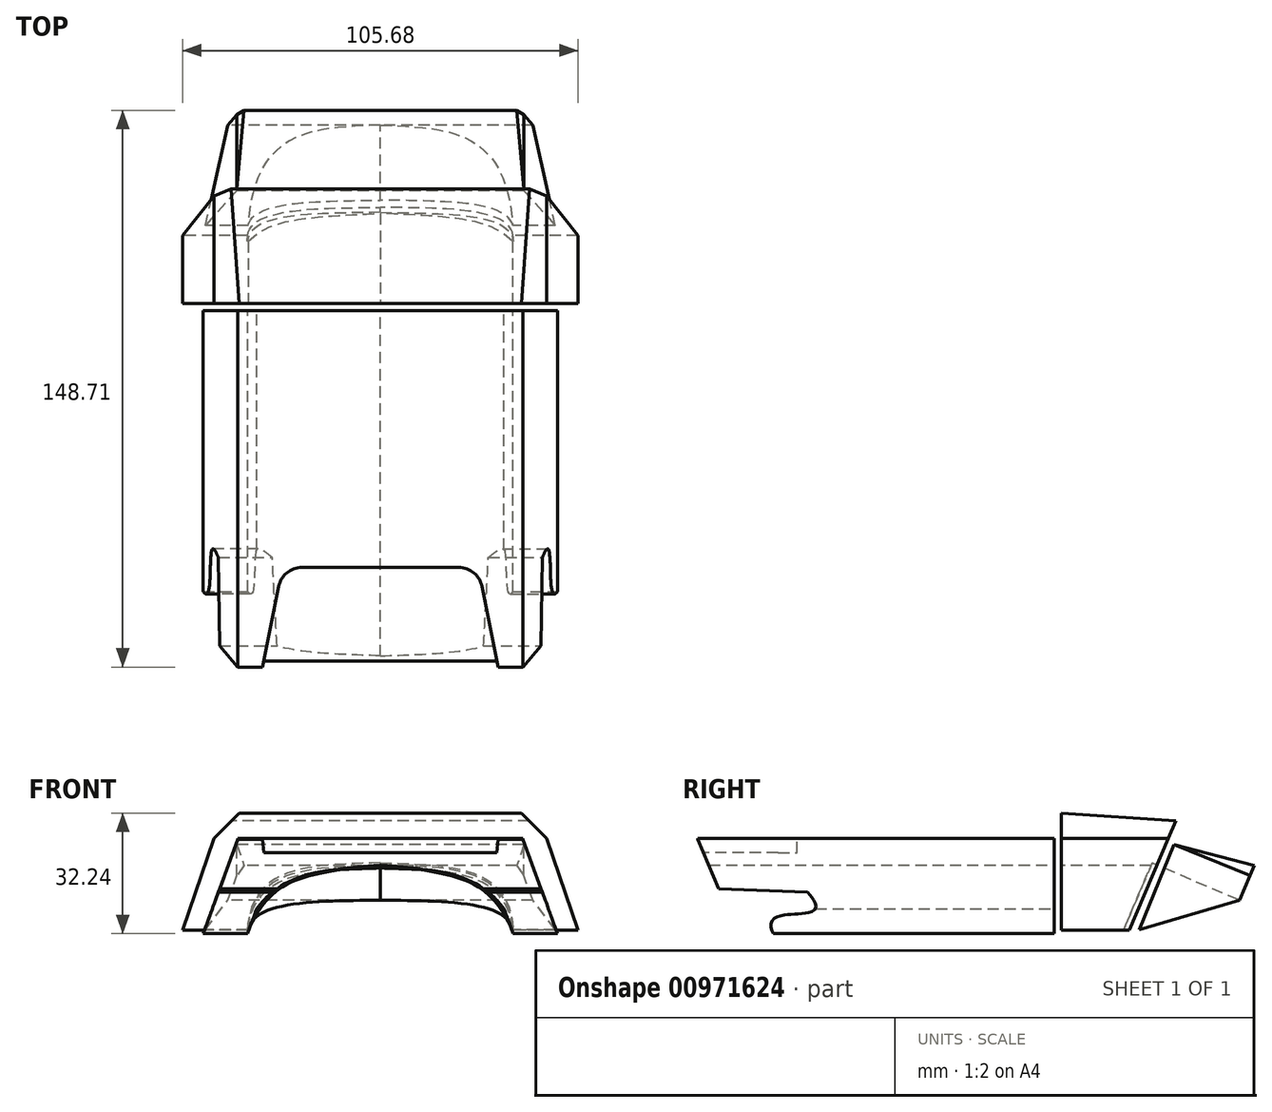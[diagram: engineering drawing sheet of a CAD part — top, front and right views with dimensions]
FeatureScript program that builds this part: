
annotation { "Feature Type Name" : "Feature", "Feature Type Description" : "" }
export const myFeature = defineFeature(function(context is Context, id is Id, definition is map)
    precondition{}
    {
        {
            var Q0;
            Q0=qCreatedBy(makeId("Top.planeOp"),FACE);
            var sketch = newSketch(context, id + "F0", { "sketchPlane" : qUnion([Q0])});
            skLineSegment(sketch, "E0.bottom", {"start": v(38.1, 47.63) * mm, "end": v(-38.1, 47.63) * mm});
            skLineSegment(sketch, "E0.top", {"start": v(38.1, -47.63) * mm, "end": v(-38.1, -47.63) * mm});
            skLineSegment(sketch, "E0.left", {"start": v(38.1, 47.63) * mm, "end": v(38.1, -47.63) * mm});
            skLineSegment(sketch, "E0.right", {"start": v(-38.1, 47.63) * mm, "end": v(-38.1, -47.63) * mm});
            skPoint(sketch, "E0.middle", {"position": v(0, 0) * mm});
            skLineSegment(sketch, "E1", {"start": v(0, -21.05) * mm, "end": v(-20.94, -21.05) * mm});
            skLineSegment(sketch, "E2", {"start": v(-27.17, -26.16) * mm, "end": v(-31.46, -47.63) * mm});
            skPoint(sketch, "E3.visualSharp", {"position": v(-26.15, -21.05) * mm});
            skArc(sketch, "E3.filletArc", {"start": v(-20.94, -21.05) * mm, "mid": v(-24.96, -22.5) * mm, "end": v(-27.17, -26.16) * mm});
            skLineSegment(sketch, "E4.MirrorCS", {"start": v(0, -21.05) * mm, "end": v(20.94, -21.05) * mm});
            skArc(sketch, "E5.MirrorCS", {"start": v(20.94, -21.05) * mm, "mid": v(24.96, -22.5) * mm, "end": v(27.17, -26.16) * mm});
            skLineSegment(sketch, "E6.MirrorCS", {"start": v(27.17, -26.16) * mm, "end": v(31.46, -47.63) * mm});
            skSolve(sketch);
        }
        {
            var Q0;
            Q0=makeQuery(id+"F0.imprint","IMPRINT",FACE,{"disambiguationData":[TD([[makeQuery(id+"F0.imprint","IMPRINT",EDGE,{"derivedFrom":sQuery(id+"F0.wireOp",EDGE,"E0.bottom")}),1.0]])]});
            var Q1;
            Q1=makeQuery(id+"F0.imprint","IMPRINT",FACE,{"disambiguationData":[TD([[makeQuery(id+"F0.imprint","IMPRINT",EDGE,{"derivedFrom":sQuery(id+"F0.wireOp",EDGE,"E1")}),1.0]])]});
            extrude(context, id + "F1", {"entities" : qUnion([Q0, Q1]), "oppositeDirection" : true, "depth" : 25.4 * mm, "offsetDistance" : 25.4 * mm, "hasDraft" : true, "draftAngle" : 20 * degree});
        }
        {
            var Q0;
            Q0=makeQuery(id+"F1.opExtrude","CAP_FACE",FACE,{"disambiguationData":[OSD([sQuery(id+"F0.wireOp",EDGE,"E0.bottom"),sQuery(id+"F0.wireOp",EDGE,"E0.top"),sQuery(id+"F0.wireOp",EDGE,"E0.left"),sQuery(id+"F0.wireOp",EDGE,"E0.right")])],"isStart":true});
            var sketch = newSketch(context, id + "F2", { "sketchPlane" : qUnion([Q0])});
            skLineSegment(sketch, "E7.bottom", {"start": v(-53.4, 47.63) * mm, "end": v(63.46, 47.63) * mm});
            skLineSegment(sketch, "E7.top", {"start": v(-53.4, 69.25) * mm, "end": v(63.46, 69.25) * mm});
            skLineSegment(sketch, "E7.left", {"start": v(-53.4, 47.63) * mm, "end": v(-53.4, 69.25) * mm});
            skLineSegment(sketch, "E7.right", {"start": v(63.46, 47.63) * mm, "end": v(63.46, 69.25) * mm});
            skLineSegment(sketch, "E8.bottom", {"start": v(-38.1, -47.63) * mm, "end": v(-66.4, -47.63) * mm});
            skLineSegment(sketch, "E8.top", {"start": v(-38.1, -70.22) * mm, "end": v(-66.4, -70.22) * mm});
            skLineSegment(sketch, "E8.left", {"start": v(-38.1, -47.63) * mm, "end": v(-38.1, -70.22) * mm});
            skLineSegment(sketch, "E8.right", {"start": v(-66.4, -47.63) * mm, "end": v(-66.4, -70.22) * mm});
            skLineSegment(sketch, "E9.bottom", {"start": v(-38.1, -47.63) * mm, "end": v(69.23, -47.63) * mm});
            skLineSegment(sketch, "E9.top", {"start": v(-38.1, -70.22) * mm, "end": v(69.23, -70.22) * mm});
            skLineSegment(sketch, "E9.right", {"start": v(69.23, -47.63) * mm, "end": v(69.23, -70.22) * mm});
            skSolve(sketch);
        }
        {
            var Q0;
            Q0=makeQuery(id+"F2.imprint","IMPRINT",FACE,{"disambiguationData":[TD([[makeQuery(id+"F2.imprint","IMPRINT",EDGE,{"derivedFrom":sQuery(id+"F2.wireOp",EDGE,"E9.top")}),1.0]])]});
            var Q1;
            Q1=makeQuery(id+"F2.imprint","IMPRINT",FACE,{"disambiguationData":[TD([[makeQuery(id+"F2.imprint","IMPRINT",EDGE,{"derivedFrom":sQuery(id+"F2.wireOp",EDGE,"E8.bottom")}),1.0]])]});
            var Q2;
            Q2=makeQuery(id+"F2.imprint","IMPRINT",FACE,{"disambiguationData":[TD([[makeQuery(id+"F2.imprint","IMPRINT",EDGE,{"derivedFrom":sQuery(id+"F2.wireOp",EDGE,"E7.top")}),-1.0]])]});
            extrude(context, id + "F3", {"entities" : qUnion([Q0, Q1, Q2]), "operationType" : NewBodyOperationType.REMOVE, "oppositeDirection" : true, "depth" : 36.07 * mm, "offsetDistance" : 25.4 * mm});
        }
        {
            var Q0;
            Q0=qCreatedBy(makeId("Right.planeOp"),FACE);
            var sketch = newSketch(context, id + "F4", { "sketchPlane" : qUnion([Q0])});
            skLineSegment(sketch, "E10", {"start": v(-48.1, -13.1) * mm, "end": v(-18.31, -14.34) * mm});
            skFitSpline(sketch, "E11", {"points": [v(-18.31, -14.34) * mm, v(-27.34, -25.66) * mm], "startDerivative": vector(28.35, -31.4) * mm, "endDerivative": vector(16.02, -30.28) * mm});
            skLineSegment(sketch, "E12", {"start": v(-48.1, -13.1) * mm, "end": v(-48.7, -27.37) * mm});
            skLineSegment(sketch, "E13", {"start": v(-48.7, -27.37) * mm, "end": v(-27.34, -25.66) * mm});
            skSolve(sketch);
        }
        {
            var Q0;
            Q0=makeQuery(id+"F4.imprint","IMPRINT",FACE,{"disambiguationData":[TD([[makeQuery(id+"F4.imprint","IMPRINT",EDGE,{"derivedFrom":sQuery(id+"F4.wireOp",EDGE,"E10")}),-1.0]])]});
            extrude(context, id + "F5", {"entities" : qUnion([Q0]), "operationType" : NewBodyOperationType.REMOVE, "endBound" : BoundingType.SYMMETRIC, "oppositeDirection" : true, "depth" : 115.32 * mm, "offsetDistance" : 25.4 * mm});
        }
        {
            var Q0;
            Q0=makeQuery(id+"F3.boolean.opBoolean","COPY",FACE,{"derivedFrom":makeQuery(id+"F3.opExtrude","SWEPT_FACE",FACE,{"disambiguationData":[OSD([sQuery(id+"F2.wireOp",EDGE,"E7.bottom")])]})});
            var sketch = newSketch(context, id + "F6", { "sketchPlane" : qUnion([Q0])});
            skLineSegment(sketch, "E14", {"start": v(-35.48, -25.4) * mm, "end": v(-33.06, -18.74) * mm});
            skFitSpline(sketch, "E15", {"points": [v(-33.06, -18.74) * mm, v(0, -7.1) * mm], "startDerivative": vector(22.23, 29.15) * mm, "endDerivative": vector(49.72, 4.16) * mm});
            skFitSpline(sketch, "E16.MirrorCS", {"points": [v(33.06, -18.74) * mm, v(0, -7.1) * mm], "startDerivative": vector(-22.23, 29.15) * mm, "endDerivative": vector(-49.72, 4.16) * mm});
            skLineSegment(sketch, "E17.MirrorCS", {"start": v(35.48, -25.4) * mm, "end": v(33.06, -18.74) * mm});
            skSolve(sketch);
        }
        {
            var Q0;
            {var subQ1=sQuery(id+"F6.wireOp",EDGE,"E14");Q0=makeQuery(id+"F6.imprint","IMPRINT",FACE,{"disambiguationData":[TD([[makeQuery(id+"F6.imprint","IMPRINT",EDGE,{"derivedFrom":subQ1}),-1.0]])]});}
            extrude(context, id + "F7", {"entities" : qUnion([Q0]), "operationType" : NewBodyOperationType.REMOVE, "oppositeDirection" : true, "depth" : 118.87 * mm, "offsetDistance" : 25.4 * mm});
        }
        {
            var Q0;
            Q0=makeQuery(id+"F0.imprint","IMPRINT",FACE,{"disambiguationData":[TD([[makeQuery(id+"F0.imprint","IMPRINT",EDGE,{"derivedFrom":sQuery(id+"F0.wireOp",EDGE,"E1")}),1.0]])]});
            extrude(context, id + "F8", {"entities" : qUnion([Q0]), "operationType" : NewBodyOperationType.REMOVE, "oppositeDirection" : true, "depth" : 3.8 * mm, "offsetDistance" : 25.4 * mm});
        }
        {
            var Q0;
            Q0=qCreatedBy(makeId("Right.planeOp"),FACE);
            var sketch = newSketch(context, id + "F9", { "sketchPlane" : qUnion([Q0])});
            skLineSegment(sketch, "E18", {"start": v(-41.34, -14.9) * mm, "end": v(-48.97, 3.04) * mm});
            skLineSegment(sketch, "E19", {"start": v(-48.97, 3.04) * mm, "end": v(-48.97, -14.74) * mm});
            skLineSegment(sketch, "E20", {"start": v(-48.97, -14.74) * mm, "end": v(-41.34, -14.9) * mm});
            skSolve(sketch);
        }
        {
            var Q0;
            Q0=makeQuery(id+"F9.imprint","IMPRINT",FACE,{"disambiguationData":[TD([[makeQuery(id+"F9.imprint","IMPRINT",EDGE,{"derivedFrom":sQuery(id+"F9.wireOp",EDGE,"E18")}),1.0]])]});
            extrude(context, id + "F10", {"entities" : qUnion([Q0]), "operationType" : NewBodyOperationType.REMOVE, "endBound" : BoundingType.SYMMETRIC, "oppositeDirection" : true, "depth" : 127.5 * mm, "offsetDistance" : 25.4 * mm});
        }
        {
            var Q0;
            Q0=qCreatedBy(makeId("Right.planeOp"),FACE);
            var sketch = newSketch(context, id + "F11", { "sketchPlane" : qUnion([Q0])});
            skLineSegment(sketch, "E21", {"start": v(49.52, 0) * mm, "end": v(49.52, 6.84) * mm});
            skLineSegment(sketch, "E22", {"start": v(49.52, 6.84) * mm, "end": v(49.52, -24.51) * mm});
            skLineSegment(sketch, "E23", {"start": v(49.52, -24.51) * mm, "end": v(67.7, -24.51) * mm});
            skLineSegment(sketch, "E24", {"start": v(67.7, -24.51) * mm, "end": v(80.14, 4.7) * mm});
            skLineSegment(sketch, "E25", {"start": v(80.14, 4.7) * mm, "end": v(49.52, 6.84) * mm});
            skSolve(sketch);
        }
        {
            var Q0;
            {var subQ2=sQuery(id+"F11.wireOp",EDGE,"E23");Q0=makeQuery(id+"F11.imprint","IMPRINT",FACE,{"disambiguationData":[TD([[makeQuery(id+"F11.imprint","IMPRINT",EDGE,{"derivedFrom":subQ2}),1.0]])]});}
            extrude(context, id + "F12", {"entities" : qUnion([Q0]), "endBound" : BoundingType.SYMMETRIC, "depth" : 108.2 * mm, "offsetDistance" : 25.4 * mm});
        }
        {
            var Q0;
            Q0=makeQuery(id+"F12.opExtrude","SWEPT_FACE",FACE,{"disambiguationData":[OSD([sQuery(id+"F11.wireOp",EDGE,"E22")])]});
            var sketch = newSketch(context, id + "F13", { "sketchPlane" : qUnion([Q0])});
            skLineSegment(sketch, "E26", {"start": v(-52.84, -24.51) * mm, "end": v(-44.4, 0) * mm});
            skLineSegment(sketch, "E27", {"start": v(-44.4, 0) * mm, "end": v(-37.75, 6.84) * mm});
            skLineSegment(sketch, "E28.MirrorCS", {"start": v(44.4, 0) * mm, "end": v(37.75, 6.84) * mm});
            skLineSegment(sketch, "E29.MirrorCS", {"start": v(52.84, -24.51) * mm, "end": v(44.4, 0) * mm});
            skSolve(sketch);
        }
        {
            var Q0;
            {var subQ4=sQuery(id+"F13.wireOp",EDGE,"E26");Q0=makeQuery(id+"F13.imprint","IMPRINT",FACE,{"disambiguationData":[TD([[makeQuery(id+"F13.imprint","IMPRINT",EDGE,{"derivedFrom":subQ4}),1.0]])]});}
            var Q1;
            {var subQ4=sQuery(id+"F13.wireOp",EDGE,"E28.MirrorCS");Q1=makeQuery(id+"F13.imprint","IMPRINT",FACE,{"disambiguationData":[TD([[makeQuery(id+"F13.imprint","IMPRINT",EDGE,{"derivedFrom":subQ4}),-1.0]])]});}
            extrude(context, id + "F14", {"entities" : qUnion([Q0, Q1]), "operationType" : NewBodyOperationType.REMOVE, "oppositeDirection" : true, "depth" : 37.85 * mm, "offsetDistance" : 25.4 * mm});
        }
        {
            var Q0;
            Q0=makeQuery(id+"F12.opExtrude","SWEPT_FACE",FACE,{"disambiguationData":[OSD([sQuery(id+"F11.wireOp",EDGE,"E22")])]});
            var sketch = newSketch(context, id + "F15", { "sketchPlane" : qUnion([Q0])});
            skFitSpline(sketch, "E30", {"points": [v(-35.31, -24.51) * mm, v(0, -7.12) * mm], "startDerivative": vector(18.12, 40.86) * mm, "endDerivative": vector(65.16, 6.34) * mm});
            skFitSpline(sketch, "E31.MirrorCS", {"points": [v(35.31, -24.51) * mm, v(0, -7.12) * mm], "startDerivative": vector(-18.12, 40.86) * mm, "endDerivative": vector(-65.16, 6.34) * mm});
            skSolve(sketch);
        }
        {
            var Q0;
            {var subQ0=sQuery(id+"F15.wireOp",EDGE,"E30");Q0=makeQuery(id+"F15.imprint","IMPRINT",FACE,{"disambiguationData":[TD([[makeQuery(id+"F15.imprint","IMPRINT",EDGE,{"derivedFrom":subQ0}),-1.0]])]});}
            extrude(context, id + "F16", {"entities" : qUnion([Q0]), "operationType" : NewBodyOperationType.REMOVE, "oppositeDirection" : true, "depth" : 51.05 * mm, "offsetDistance" : 25.4 * mm});
        }
        {
            var Q0;
            Q0=qCreatedBy(makeId("Right.planeOp"),FACE);
            var sketch = newSketch(context, id + "F17", { "sketchPlane" : qUnion([Q0])});
            skLineSegment(sketch, "E32", {"start": v(70.33, -24.27) * mm, "end": v(79.63, -1.57) * mm});
            skLineSegment(sketch, "E33", {"start": v(79.63, -1.57) * mm, "end": v(101.08, -7.2) * mm});
            skLineSegment(sketch, "E34", {"start": v(101.08, -7.2) * mm, "end": v(97.15, -16.41) * mm});
            skLineSegment(sketch, "E35", {"start": v(97.15, -16.41) * mm, "end": v(70.33, -24.27) * mm});
            skSolve(sketch);
        }
        {
            var Q0;
            Q0=makeQuery(id+"F17.imprint","IMPRINT",FACE,{"disambiguationData":[TD([[makeQuery(id+"F17.imprint","IMPRINT",EDGE,{"derivedFrom":sQuery(id+"F17.wireOp",EDGE,"E32")}),-1.0]])]});
            extrude(context, id + "F18", {"entities" : qUnion([Q0]), "endBound" : BoundingType.SYMMETRIC, "depth" : 93.47 * mm, "offsetDistance" : 25.4 * mm});
        }
        {
            var Q0;
            Q0=makeQuery(id+"F18.opExtrude","SWEPT_FACE",FACE,{"disambiguationData":[OSD([sQuery(id+"F17.wireOp",EDGE,"E32")])]});
            var sketch = newSketch(context, id + "F19", { "sketchPlane" : qUnion([Q0])});
            skLineSegment(sketch, "E36", {"start": v(-38.35, 28.75) * mm, "end": v(-46.74, 4.22) * mm});
            skLineSegment(sketch, "E37", {"start": v(-46.74, 4.22) * mm, "end": v(-46.74, 28.75) * mm});
            skLineSegment(sketch, "E38", {"start": v(-46.74, 28.75) * mm, "end": v(-38.35, 28.75) * mm});
            skLineSegment(sketch, "E39.MirrorCS", {"start": v(46.74, 28.75) * mm, "end": v(38.35, 28.75) * mm});
            skLineSegment(sketch, "E40.MirrorCS", {"start": v(38.35, 28.75) * mm, "end": v(46.74, 4.22) * mm});
            skLineSegment(sketch, "E41.MirrorCS", {"start": v(46.74, 4.22) * mm, "end": v(46.74, 28.75) * mm});
            skLineSegment(sketch, "E42", {"start": v(-38.35, 28.75) * mm, "end": v(-35.63, 32.8) * mm});
            skLineSegment(sketch, "E43", {"start": v(-35.63, 32.8) * mm, "end": v(-46.74, 33.83) * mm});
            skLineSegment(sketch, "E44", {"start": v(-46.74, 33.83) * mm, "end": v(-46.74, 28.75) * mm});
            skLineSegment(sketch, "E45", {"start": v(38.35, 28.75) * mm, "end": v(35.96, 32.49) * mm});
            skLineSegment(sketch, "E46", {"start": v(35.96, 32.49) * mm, "end": v(51.54, 32.49) * mm});
            skLineSegment(sketch, "E47", {"start": v(51.54, 32.49) * mm, "end": v(46.74, 28.75) * mm});
            skSolve(sketch);
        }
        {
            var Q0;
            Q0=makeQuery(id+"F19.imprint","IMPRINT",FACE,{"disambiguationData":[TD([[makeQuery(id+"F19.imprint","IMPRINT",EDGE,{"derivedFrom":sQuery(id+"F19.wireOp",EDGE,"E36")}),-1.0]])]});
            var Q1;
            Q1=makeQuery(id+"F19.imprint","IMPRINT",FACE,{"disambiguationData":[TD([[makeQuery(id+"F19.imprint","IMPRINT",EDGE,{"derivedFrom":sQuery(id+"F19.wireOp",EDGE,"E39.MirrorCS")}),1.0]])]});
            var Q2;
            Q2=makeQuery(id+"F19.imprint","IMPRINT",FACE,{"disambiguationData":[TD([[makeQuery(id+"F19.imprint","IMPRINT",EDGE,{"derivedFrom":sQuery(id+"F19.wireOp",EDGE,"E38")}),-1.0]])]});
            var Q3;
            Q3=makeQuery(id+"F19.imprint","IMPRINT",FACE,{"disambiguationData":[TD([[makeQuery(id+"F19.imprint","IMPRINT",EDGE,{"derivedFrom":sQuery(id+"F19.wireOp",EDGE,"E39.MirrorCS")}),-1.0]])]});
            extrude(context, id + "F20", {"entities" : qUnion([Q0, Q1, Q2, Q3]), "operationType" : NewBodyOperationType.REMOVE, "oppositeDirection" : true, "depth" : 25.4 * mm, "offsetDistance" : 25.4 * mm});
        }
        {
            var Q0;
            Q0=makeQuery(id+"F18.opExtrude","SWEPT_FACE",FACE,{"disambiguationData":[OSD([sQuery(id+"F17.wireOp",EDGE,"E34")])]});
            var sketch = newSketch(context, id + "F21", { "sketchPlane" : qUnion([Q0])});
            skFitSpline(sketch, "E48", {"points": [v(0, 23) * mm, v(-35.54, 1.92) * mm], "startDerivative": vector(-53.86, -2.03) * mm, "endDerivative": vector(0.02, -63.23) * mm});
            skLineSegment(sketch, "E49", {"start": v(-35.54, 1.92) * mm, "end": v(0, 1.92) * mm});
            skFitSpline(sketch, "E50.MirrorCS", {"points": [v(0, 23) * mm, v(35.54, 1.92) * mm], "startDerivative": vector(53.86, -2.03) * mm, "endDerivative": vector(-0.02, -63.23) * mm});
            skLineSegment(sketch, "E51.MirrorCS", {"start": v(35.54, 1.92) * mm, "end": v(0, 1.92) * mm});
            skSolve(sketch);
        }
        {
            var Q0;
            Q0=makeQuery(id+"F21.imprint","IMPRINT",FACE,{"disambiguationData":[TD([[makeQuery(id+"F21.imprint","IMPRINT",EDGE,{"derivedFrom":sQuery(id+"F21.wireOp",EDGE,"E48")}),1.0]])]});
            extrude(context, id + "F22", {"entities" : qUnion([Q0]), "operationType" : NewBodyOperationType.REMOVE, "oppositeDirection" : true, "depth" : 25.4 * mm, "offsetDistance" : 25.4 * mm});
        }
    });
